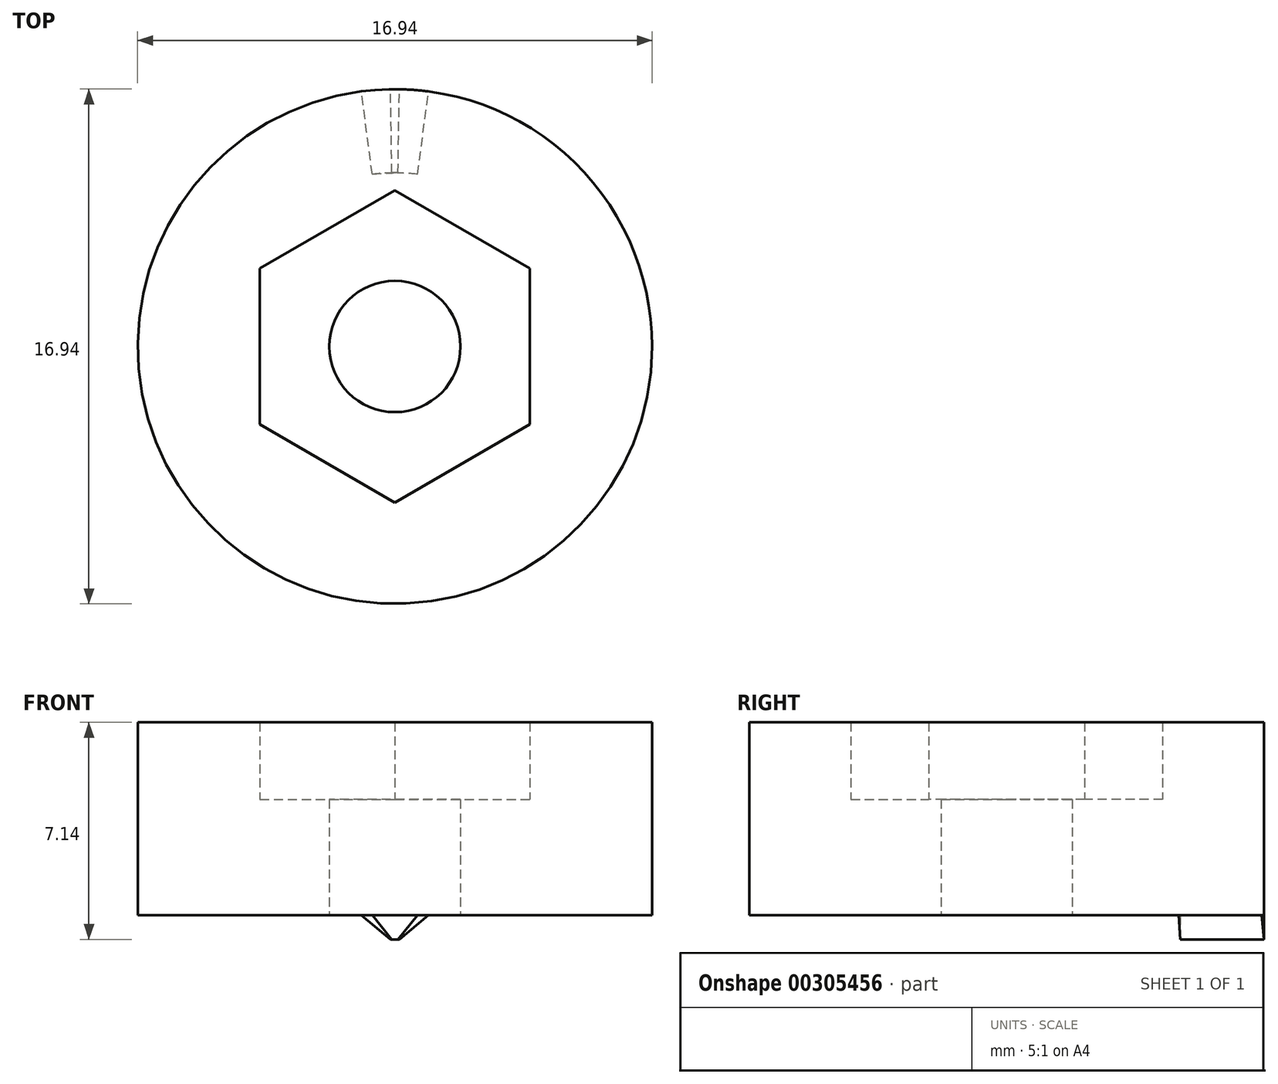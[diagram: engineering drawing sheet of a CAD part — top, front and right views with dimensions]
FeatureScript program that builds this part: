
annotation { "Feature Type Name" : "Feature", "Feature Type Description" : "" }
export const myFeature = defineFeature(function(context is Context, id is Id, definition is map)
    precondition{}
    {
        {
            var Q0;
            Q0=qCreatedBy(makeId("Top.planeOp"),FACE);
            var sketch = newSketch(context, id + "F0", { "sketchPlane" : qUnion([Q0])});
            skCircle(sketch, "E0.cCircle", {"center": v(0, 0) * mm, "radius": 4.45 * mm, "construction": true});
            skLineSegment(sketch, "E0.0", {"start": v(4.45, 2.57) * mm, "end": v(4.45, -2.57) * mm});
            skLineSegment(sketch, "E0.1", {"start": v(4.44, -2.57) * mm, "end": v(0, -5.13) * mm});
            skLineSegment(sketch, "E0.2", {"start": v(0, -5.13) * mm, "end": v(-4.45, -2.57) * mm});
            skLineSegment(sketch, "E0.3", {"start": v(-4.45, -2.57) * mm, "end": v(-4.45, 2.57) * mm});
            skLineSegment(sketch, "E0.4", {"start": v(-4.45, 2.57) * mm, "end": v(0, 5.13) * mm});
            skLineSegment(sketch, "E0.5", {"start": v(0, 5.13) * mm, "end": v(4.45, 2.57) * mm});
            skPoint(sketch, "E0.0.midPoint", {"position": v(4.45, 0) * mm});
            skCircle(sketch, "E1", {"center": v(0, 0) * mm, "radius": 8.47 * mm});
            skCircle(sketch, "E2", {"center": v(0, 0) * mm, "radius": 2.16 * mm});
            skSolve(sketch);
        }
        {
            var Q0;
            Q0=makeQuery(id+"F0.imprint","IMPRINT",FACE,{"disambiguationData":[TD([[makeQuery(id+"F0.imprint","IMPRINT",EDGE,{"derivedFrom":sQuery(id+"F0.wireOp",EDGE,"E0.0")}),-1.0]])]});
            extrude(context, id + "F1", {"entities" : qUnion([Q0]), "depth" : 3.8 * mm});
        }
        {
            var Q0;
            Q0 = qSketchRegion(id + "F0", true);
            extrude(context, id + "F2", {"entities" : qUnion([Q0]), "operationType" : NewBodyOperationType.ADD, "depth" : 6.35 * mm});
        }
        {
            var Q0;
            Q0=makeQuery(id+"F0.imprint","IMPRINT",FACE,{"disambiguationData":[TD([[makeQuery(id+"F0.imprint","IMPRINT",EDGE,{"derivedFrom":sQuery(id+"F0.wireOp",EDGE,"E0.0")}),1.0]])]});
            var sketch = newSketch(context, id + "F3", { "sketchPlane" : qUnion([Q0])});
            skArc(sketch, "E3.0", {"start": v(1.1, 8.4) * mm, "mid": v(0, 8.47) * mm, "end": v(-1.1, 8.4) * mm});
            skArc(sketch, "E4", {"start": v(0.75, 5.67) * mm, "mid": v(0, 5.72) * mm, "end": v(-0.75, 5.67) * mm});
            skLineSegment(sketch, "E5", {"start": v(0.75, 5.67) * mm, "end": v(1.1, 8.4) * mm});
            skLineSegment(sketch, "E6.MirrorCS", {"start": v(-0.75, 5.67) * mm, "end": v(-1.1, 8.4) * mm});
            skSolve(sketch);
        }
        {
            var Q0;
            Q0=makeQuery(id+"F0.imprint","IMPRINT",FACE,{"disambiguationData":[TD([[makeQuery(id+"F0.imprint","IMPRINT",EDGE,{"derivedFrom":sQuery(id+"F0.wireOp",EDGE,"E0.0")}),1.0]])]});
            cPlane(context, id + "F4", {"entities" : qUnion([Q0]), "cplaneType" : CPlaneType.OFFSET, "offset" : 0.8 * mm, "oppositeDirection" : true, "width" : 152.4 * mm, "height" : 152.4 * mm});
        }
        {
            var Q0;
            Q0=qCreatedBy(id+"F4.planeOp",FACE);
            var sketch = newSketch(context, id + "F5", { "sketchPlane" : qUnion([Q0])});
            skArc(sketch, "E7.0", {"start": v(0.15, 8.47) * mm, "mid": v(0, 8.47) * mm, "end": v(-0.15, 8.47) * mm});
            skArc(sketch, "E8.0", {"start": v(0.1, 5.71) * mm, "mid": v(0, 5.72) * mm, "end": v(-0.1, 5.71) * mm});
            skLineSegment(sketch, "E9", {"start": v(0.1, 5.71) * mm, "end": v(0.15, 8.47) * mm});
            skLineSegment(sketch, "E10.MirrorCS", {"start": v(-0.1, 5.71) * mm, "end": v(-0.15, 8.47) * mm});
            skPoint(sketch, "E11.orphan", {"position": v(0.75, 5.67) * mm});
            skPoint(sketch, "E12.orphan", {"position": v(-0.75, 5.67) * mm});
            skSolve(sketch);
        }
        {
            var Q1;
            Q1=makeQuery(id+"F3.imprint","IMPRINT",FACE,{"disambiguationData":[TD([[makeQuery(id+"F3.imprint","IMPRINT",EDGE,{"derivedFrom":sQuery(id+"F3.wireOp",EDGE,"E3.0")}),1.0]])]});
            var Q2;
            Q2=makeQuery(id+"F5.imprint","IMPRINT",FACE,{"disambiguationData":[TD([[makeQuery(id+"F5.imprint","IMPRINT",EDGE,{"derivedFrom":sQuery(id+"F5.wireOp",EDGE,"E7.0")}),1.0]])]});
            loft(context, id + "F6", {"operationType" : NewBodyOperationType.ADD, "sheetProfilesArray" : [{ "sheetProfileEntities" : qUnion([Q1]) }, { "sheetProfileEntities" : qUnion([Q2]) }]});
        }
    });
